# Revit family: DTI_A3-SKL&RSO
name_source: partatom
category: Windows
revit_build: Autodesk Revit 2016 (Build: 20150220_1215(x64)
units: mm (PartAtom-declared; Revit-internal decimal feet)

## family parameters
Always vertical = Yes
Cut with Voids When Loaded = No
Host = Wall
OmniClass Number = 23.30.20.00
OmniClass Title = Windows
Room Calculation Point = No
Shared = No

## types (1)
- A3 SKL&RSO
    Cill Height = 44 mm  [stored 0.144357 ft]
    Default Sill Height = 0 mm  [stored 0 ft]
    Door Frame Material = Meranti
    Frame Width = 74 mm  [stored 0.242782 ft]
    Height = 2007 mm
    Manufacturer = Swartland Doors & Windows
    Model = SKSO
    Top Rail Height = 81 mm  [stored 0.265748 ft]
    Type Comments = Cape Culture Side Light SKSO L& R
    URL = www.swartland.co.za
    Wall Closure = By host
    Width = 493 mm  [stored 1.61745 ft]

note: [stored X ft] marks values corroborated as IEEE doubles in the binary element streams (Revit-internal decimal feet)

## geometry (parser evidence)
native form markers: Blend x18, Sweep x3
no freeform markers — native parametric forms only
